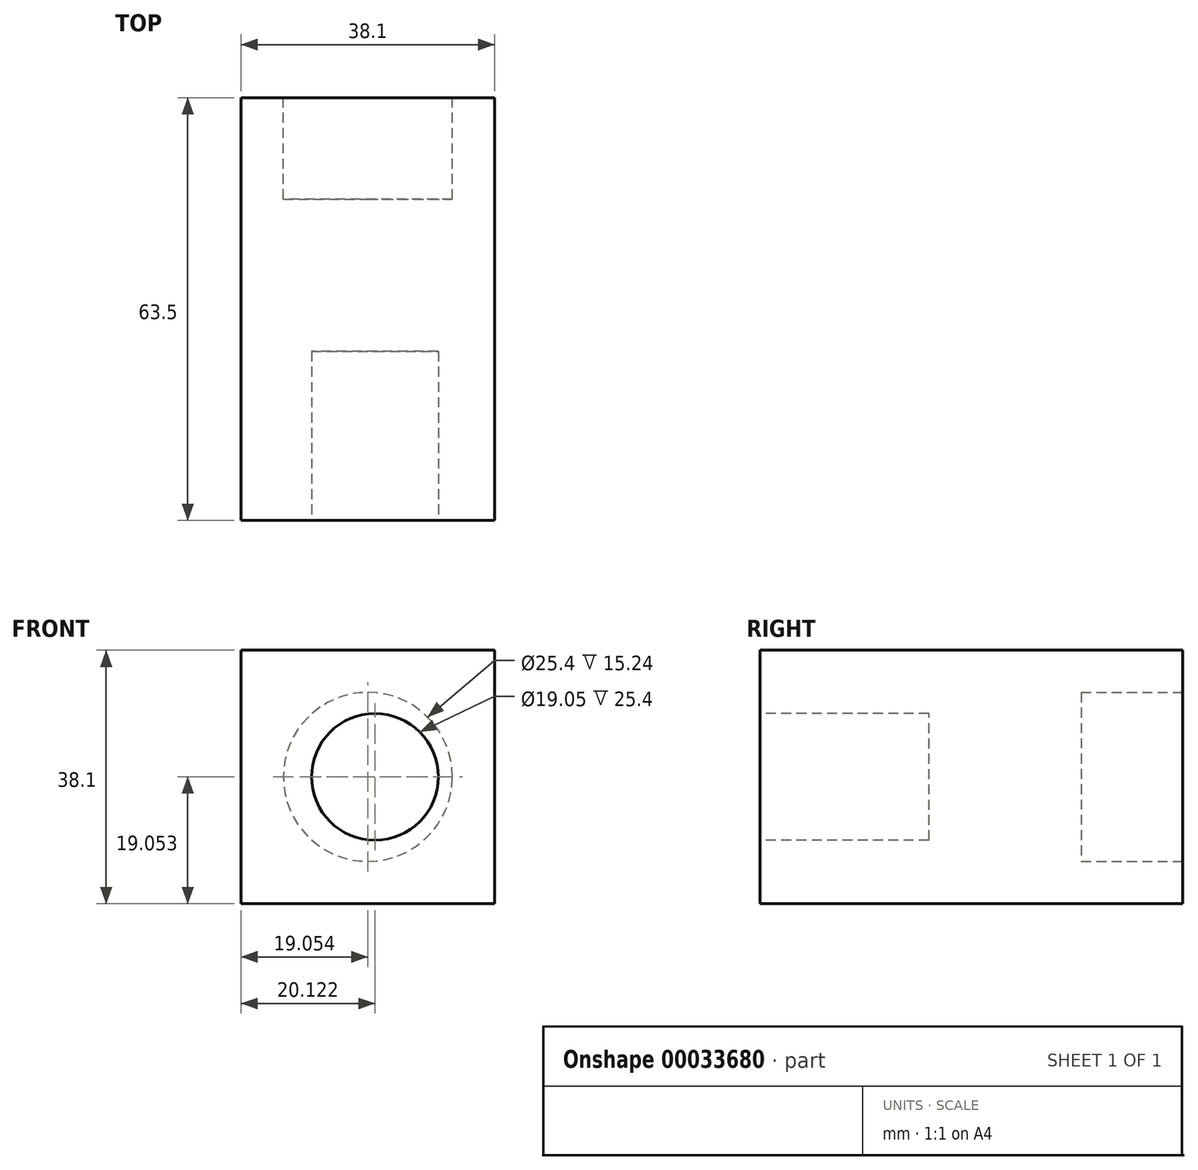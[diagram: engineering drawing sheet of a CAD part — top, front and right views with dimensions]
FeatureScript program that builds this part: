
annotation { "Feature Type Name" : "Feature", "Feature Type Description" : "" }
export const myFeature = defineFeature(function(context is Context, id is Id, definition is map)
    precondition{}
    {
        {
            var Q0;
            Q0=qCreatedBy(makeId("Front.planeOp"),FACE);
            var sketch = newSketch(context, id + "F0", { "sketchPlane" : qUnion([Q0])});
            skLineSegment(sketch, "E0.bottom", {"start": v(-25.86, 22.1) * mm, "end": v(12.24, 22.1) * mm});
            skLineSegment(sketch, "E0.top", {"start": v(-25.86, -16) * mm, "end": v(12.24, -16) * mm});
            skLineSegment(sketch, "E0.left", {"start": v(-25.86, 22.1) * mm, "end": v(-25.86, -16) * mm});
            skLineSegment(sketch, "E0.right", {"start": v(12.24, 22.1) * mm, "end": v(12.24, -16) * mm});
            skLineSegment(sketch, "E1", {"start": v(-6.8, 22.1) * mm, "end": v(-6.8, -16) * mm});
            skLineSegment(sketch, "E2", {"start": v(12.24, 3.05) * mm, "end": v(-25.86, 3.05) * mm});
            skSolve(sketch);
        }
        {
            var Q0;
            Q0 = qSketchRegion(id + "F0", true);
            extrude(context, id + "F1", {"entities" : qUnion([Q0]), "depth" : 63.5 * mm});
        }
        {
            var Q0;
            Q0=makeQuery(id+"F1.opExtrude","CAP_FACE",FACE,{"disambiguationData":[OSD([sQuery(id+"F0.wireOp",EDGE,"E0.bottom"),sQuery(id+"F0.wireOp",EDGE,"E0.top"),sQuery(id+"F0.wireOp",EDGE,"E0.left"),sQuery(id+"F0.wireOp",EDGE,"E0.right")])],"isStart":true});
            var sketch = newSketch(context, id + "F2", { "sketchPlane" : qUnion([Q0])});
            skCircle(sketch, "E3", {"center": v(6.8, 3.05) * mm, "radius": 12.7 * mm});
            skPoint(sketch, "E4.orphan", {"position": v(-12.24, 3.05) * mm});
            skPoint(sketch, "E5.start.orphan", {"position": v(6.8, 22.1) * mm});
            skPoint(sketch, "E6.trimOffspring.end.orphan", {"position": v(6.8, -16) * mm});
            skSolve(sketch);
        }
        {
            var Q0;
            Q0=makeQuery(id+"F2.imprint","IMPRINT",FACE,{"disambiguationData":[TD([[makeQuery(id+"F2.imprint","IMPRINT",EDGE,{"derivedFrom":sQuery(id+"F2.wireOp",EDGE,"E3")}),1.0]])]});
            extrude(context, id + "F3", {"entities" : qUnion([Q0]), "operationType" : NewBodyOperationType.REMOVE, "oppositeDirection" : true, "depth" : 15.24 * mm});
        }
        {
            var Q0;
            Q0=makeQuery(id+"F1.opExtrude","CAP_FACE",FACE,{"disambiguationData":[OSD([sQuery(id+"F0.wireOp",EDGE,"E0.bottom"),sQuery(id+"F0.wireOp",EDGE,"E0.top"),sQuery(id+"F0.wireOp",EDGE,"E0.left"),sQuery(id+"F0.wireOp",EDGE,"E0.right")])],"isStart":false});
            var sketch = newSketch(context, id + "F4", { "sketchPlane" : qUnion([Q0])});
            skCircle(sketch, "E7", {"center": v(-5.74, 3.05) * mm, "radius": 9.53 * mm});
            skPoint(sketch, "E8.orphan", {"position": v(-5.74, 22.1) * mm});
            skPoint(sketch, "E9.end.orphan", {"position": v(-5.74, -16) * mm});
            skPoint(sketch, "E10.trimOffspring.end.orphan", {"position": v(12.24, 3.05) * mm});
            skPoint(sketch, "E11.start.orphan", {"position": v(-25.86, 3.05) * mm});
            skSolve(sketch);
        }
        {
            var Q0;
            Q0=makeQuery(id+"F4.imprint","IMPRINT",FACE,{"disambiguationData":[TD([[makeQuery(id+"F4.imprint","IMPRINT",EDGE,{"derivedFrom":sQuery(id+"F4.wireOp",EDGE,"E7")}),1.0]])]});
            extrude(context, id + "F5", {"entities" : qUnion([Q0]), "operationType" : NewBodyOperationType.REMOVE, "oppositeDirection" : true, "depth" : 25.4 * mm});
        }
    });
